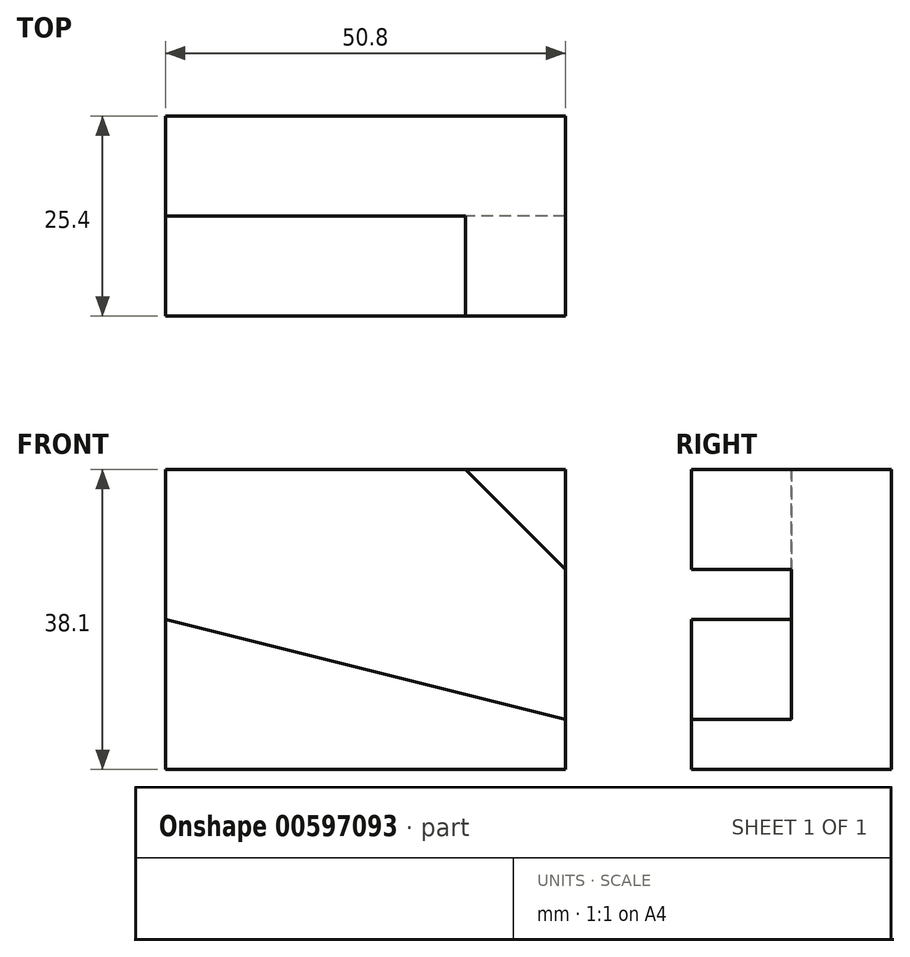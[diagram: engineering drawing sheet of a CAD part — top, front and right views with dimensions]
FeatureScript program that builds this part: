
annotation { "Feature Type Name" : "Feature", "Feature Type Description" : "" }
export const myFeature = defineFeature(function(context is Context, id is Id, definition is map)
    precondition{}
    {
        {
            var Q0;
            Q0=qCreatedBy(makeId("Front.planeOp"),FACE);
            var sketch = newSketch(context, id + "F0", { "sketchPlane" : qUnion([Q0])});
            skLineSegment(sketch, "E0", {"start": v(-72.25, 74.1) * mm, "end": v(-72.25, 36) * mm});
            skLineSegment(sketch, "E1", {"start": v(-72.25, 36) * mm, "end": v(-21.45, 36) * mm});
            skLineSegment(sketch, "E2", {"start": v(-21.45, 36) * mm, "end": v(-21.45, 74.1) * mm});
            skLineSegment(sketch, "E3", {"start": v(-21.45, 74.1) * mm, "end": v(-72.25, 74.1) * mm});
            skSolve(sketch);
        }
        {
            var Q0;
            Q0=makeQuery(id+"F0.imprint","IMPRINT",FACE,{"disambiguationData":[TD([[makeQuery(id+"F0.imprint","IMPRINT",EDGE,{"derivedFrom":sQuery(id+"F0.wireOp",EDGE,"E0")}),1.0]])]});
            extrude(context, id + "F1", {"entities" : qUnion([Q0]), "depth" : 12.7 * mm, "offsetDistance" : 25.4 * mm});
        }
        {
            var Q0;
            Q0=makeQuery(id+"F1.opExtrude","CAP_FACE",FACE,{"disambiguationData":[OSD([sQuery(id+"F0.wireOp",EDGE,"E0"),sQuery(id+"F0.wireOp",EDGE,"E1"),sQuery(id+"F0.wireOp",EDGE,"E2"),sQuery(id+"F0.wireOp",EDGE,"E3")])],"isStart":false});
            var sketch = newSketch(context, id + "F2", { "sketchPlane" : qUnion([Q0])});
            skLineSegment(sketch, "E4", {"start": v(-72.25, 55.05) * mm, "end": v(-72.25, 36) * mm});
            skLineSegment(sketch, "E5", {"start": v(-72.25, 36) * mm, "end": v(-21.45, 36) * mm});
            skLineSegment(sketch, "E6", {"start": v(-21.45, 36) * mm, "end": v(-21.45, 42.35) * mm});
            skLineSegment(sketch, "E7", {"start": v(-21.45, 42.35) * mm, "end": v(-72.25, 55.05) * mm});
            skSolve(sketch);
        }
        {
            var Q0;
            Q0=makeQuery(id+"F2.imprint","IMPRINT",FACE,{"disambiguationData":[TD([[makeQuery(id+"F2.imprint","IMPRINT",EDGE,{"derivedFrom":sQuery(id+"F2.wireOp",EDGE,"E4")}),1.0]])]});
            extrude(context, id + "F3", {"entities" : qUnion([Q0]), "operationType" : NewBodyOperationType.ADD, "depth" : 12.7 * mm, "offsetDistance" : 25.4 * mm});
        }
        {
            var Q0;
            Q0=makeQuery(id+"F1.opExtrude","CAP_FACE",FACE,{"disambiguationData":[OSD([sQuery(id+"F0.wireOp",EDGE,"E0"),sQuery(id+"F0.wireOp",EDGE,"E1"),sQuery(id+"F0.wireOp",EDGE,"E2"),sQuery(id+"F0.wireOp",EDGE,"E3")])],"isStart":false});
            var sketch = newSketch(context, id + "F4", { "sketchPlane" : qUnion([Q0])});
            skLineSegment(sketch, "E8", {"start": v(-21.45, 61.4) * mm, "end": v(-34.15, 74.1) * mm});
            skLineSegment(sketch, "E9", {"start": v(-34.15, 74.1) * mm, "end": v(-21.45, 74.1) * mm});
            skLineSegment(sketch, "E10", {"start": v(-21.45, 74.1) * mm, "end": v(-21.45, 61.4) * mm});
            skSolve(sketch);
        }
        {
            var Q0;
            Q0=makeQuery(id+"F4.imprint","IMPRINT",FACE,{"disambiguationData":[TD([[makeQuery(id+"F4.imprint","IMPRINT",EDGE,{"derivedFrom":sQuery(id+"F4.wireOp",EDGE,"E8")}),-1.0]])]});
            extrude(context, id + "F5", {"entities" : qUnion([Q0]), "operationType" : NewBodyOperationType.ADD, "depth" : 12.7 * mm, "offsetDistance" : 25.4 * mm});
        }
    });
